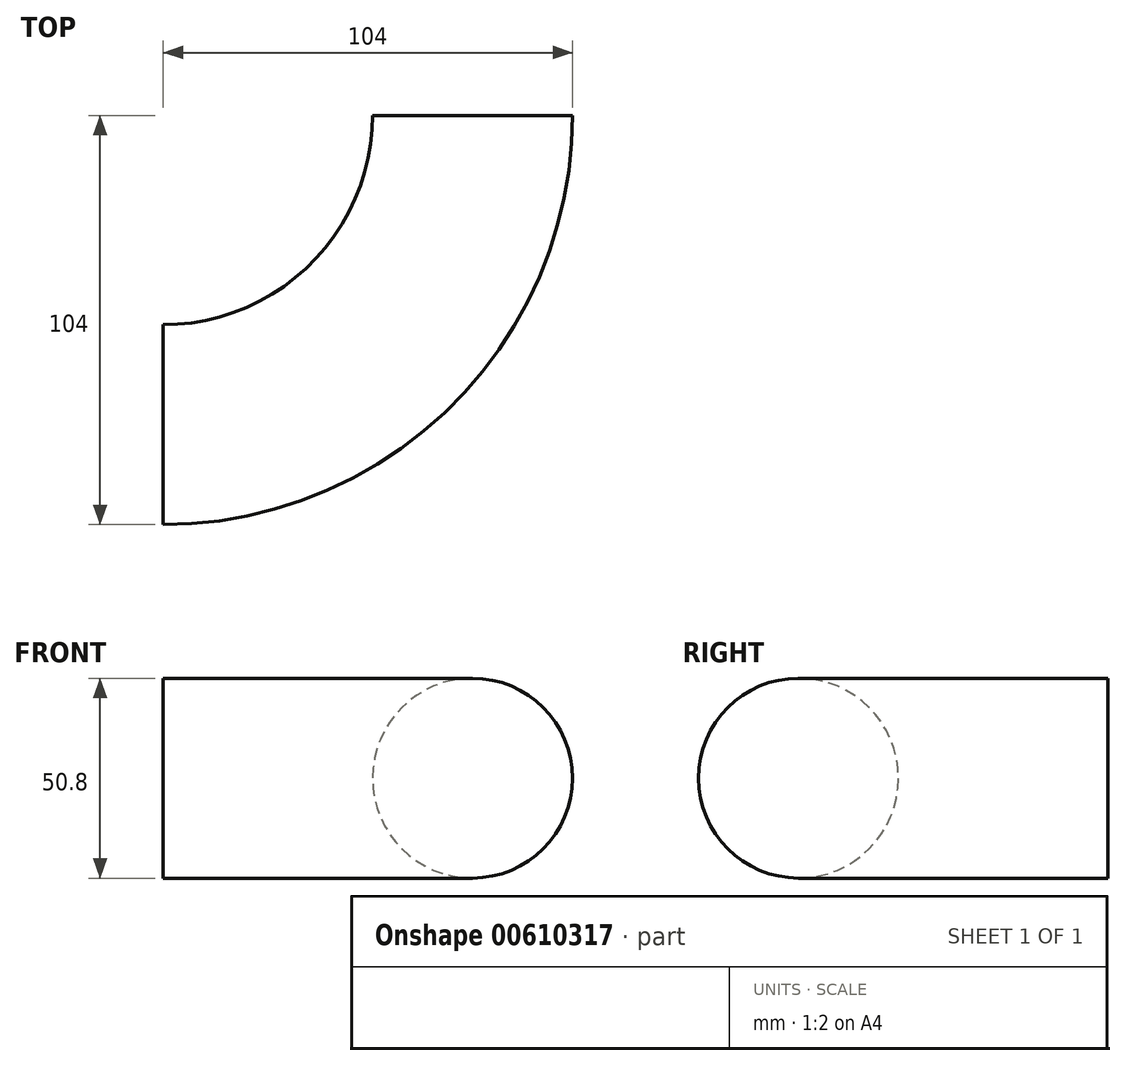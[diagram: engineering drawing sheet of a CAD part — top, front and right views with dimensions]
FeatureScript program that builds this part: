
annotation { "Feature Type Name" : "Feature", "Feature Type Description" : "" }
export const myFeature = defineFeature(function(context is Context, id is Id, definition is map)
    precondition{}
    {
        {
            var Q0;
            Q0=qCreatedBy(makeId("Top.planeOp"),FACE);
            var sketch = newSketch(context, id + "F0", { "sketchPlane" : qUnion([Q0])});
            skArc(sketch, "E0", {"start": v(0, -78.64) * mm, "mid": v(55.6, -55.6) * mm, "end": v(78.64, 0) * mm});
            skSolve(sketch);
        }
        {
            var Q0;
            Q0=qCreatedBy(makeId("Right.planeOp"),FACE);
            var Q1;
            Q1=sQuery(id+"F0.wireOp",VERTEX,"E0.start");
            cPlane(context, id + "F1", {"entities" : qUnion([Q0, Q1]), "cplaneType" : CPlaneType.PLANE_POINT, "offset" : 25.4 * mm, "width" : 152.4 * mm, "height" : 152.4 * mm});
        }
        {
            var Q0;
            Q0=qCreatedBy(id+"F1.planeOp",FACE);
            var sketch = newSketch(context, id + "F2", { "sketchPlane" : qUnion([Q0])});
            skCircle(sketch, "E1", {"center": v(-78.6, 0) * mm, "radius": 23.3 * mm});
            skCircle(sketch, "E2", {"center": v(-78.6, 0) * mm, "radius": 25.4 * mm});
            skSolve(sketch);
        }
        {
            var Q0;
            Q0=makeQuery(id+"F2.imprint","IMPRINT",FACE,{"disambiguationData":[TD([[makeQuery(id+"F2.imprint","IMPRINT",EDGE,{"derivedFrom":sQuery(id+"F2.wireOp",EDGE,"E1")}),1.0]])]});
            var Q1;
            Q1=makeQuery(id+"F2.imprint","IMPRINT",FACE,{"disambiguationData":[TD([[makeQuery(id+"F2.imprint","IMPRINT",EDGE,{"derivedFrom":sQuery(id+"F2.wireOp",EDGE,"E1")}),-1.0]])]});
            var Q2;
            Q2=sQuery(id+"F0.wireOp",EDGE,"E0");
            sweep(context, id + "F3", {"profiles" : qUnion([Q0, Q1]), "path" : qUnion([Q2])});
        }
    });
